# Revit family: AVA_AVD_Actuator_PN25_RFA_1
name_source: partatom
category: Pipe Accessories
units: mm (PartAtom-declared; Revit-internal decimal feet)

## family parameters
Always vertical = Yes
Cut with Voids When Loaded = No
OmniClass Number = 23.65.55.14.17
OmniClass Title = Adjusting/Controlling Valves for Liquid Services
Part Type = Normal
Round Connector Dimension = Use Diameter
Shared = No
Work Plane-Based = No

## types (2) — shared parameters
Actuator size = 54.0 cm²
Body Material = Danfoss Stainless Steel
Description = Spring Actuator
IfcExportAs = IfcValveType
IfcExportType = AVA_AVD_Actuator
L = 125 mm  [stored 0.410105 ft]
Manufacturer = Danfoss
Nominal Pressure = PN 25
URL = https://store.danfoss.com
W = 125 mm  [stored 0.410105 ft]

## per-type parameters (varying)
| type | Differential Pressure Setting Range | H | Higher dP | Lower dP | Model | Model Type | Spring Colour |
| AVA_AVD_Actuator_PN25_dP1-5bar_003H6844 | 1-5 bar | 156 mm | No | Yes | 003H6844 | AVA_AVD_Actuator_PN25_dP1-5bar | Danfoss Steel Paint Blue (Spring) |
| AVA_AVD_Actuator_PN25_dP3-12bar_003H6845 | 3-12 bar | 200 mm | Yes | No | 003H6845 | AVA_AVD_Actuator_PN25_dP3-12bar | Danfoss Steel Paint Black (Spring) |

note: [stored X ft] marks values corroborated as IEEE doubles in the binary element streams (Revit-internal decimal feet)

## geometry (parser evidence)
native form markers: Sweep x2
no freeform markers — native parametric forms only
